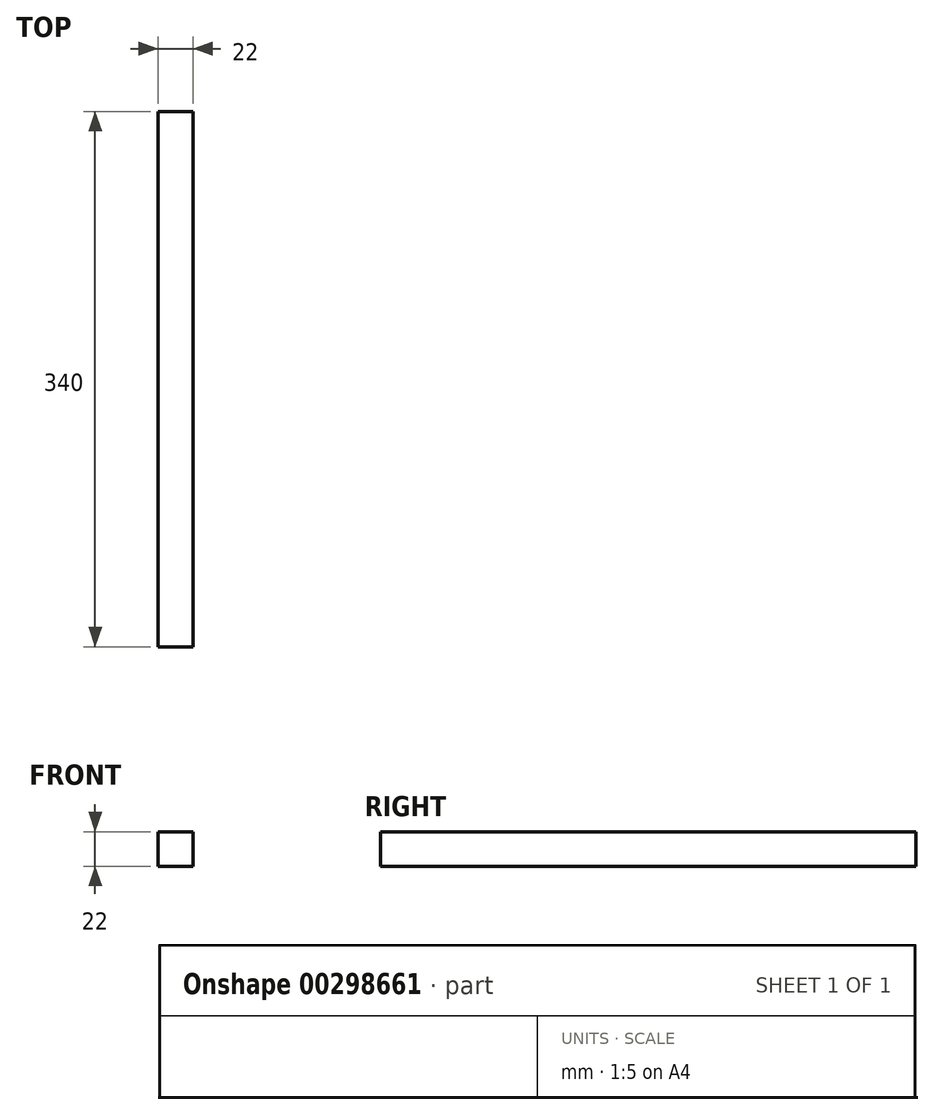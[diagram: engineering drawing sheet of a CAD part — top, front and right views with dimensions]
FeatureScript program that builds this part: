
annotation { "Feature Type Name" : "Feature", "Feature Type Description" : "" }
export const myFeature = defineFeature(function(context is Context, id is Id, definition is map)
    precondition{}
    {
        {
            var Q0;
            Q0=qCreatedBy(makeId("Front.planeOp"),FACE);
            var sketch = newSketch(context, id + "F0", { "sketchPlane" : qUnion([Q0])});
            skLineSegment(sketch, "E0.bottom", {"start": v(-11, 11) * mm, "end": v(11, 11) * mm});
            skLineSegment(sketch, "E0.top", {"start": v(-11, -11) * mm, "end": v(11, -11) * mm});
            skLineSegment(sketch, "E0.left", {"start": v(-11, 11) * mm, "end": v(-11, -11) * mm});
            skLineSegment(sketch, "E0.right", {"start": v(11, 11) * mm, "end": v(11, -11) * mm});
            skLineSegment(sketch, "E1", {"start": v(0, 0) * mm, "end": v(42.2, 0) * mm, "construction": true});
            skLineSegment(sketch, "E2", {"start": v(0, 0) * mm, "end": v(0, 29.25) * mm, "construction": true});
            skSolve(sketch);
        }
        {
            var Q0;
            Q0 = qSketchRegion(id + "F0", true);
            extrude(context, id + "F1", {"entities" : qUnion([Q0]), "oppositeDirection" : true, "depth" : 340 * mm});
        }
    });
